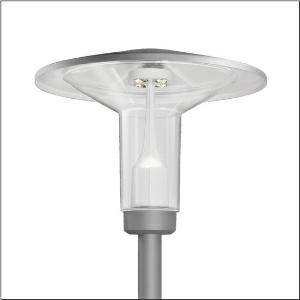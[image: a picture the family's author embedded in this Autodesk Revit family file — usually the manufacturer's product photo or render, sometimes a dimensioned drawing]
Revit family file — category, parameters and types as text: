
# Revit family: laterne_iq___st1_2a_5xa5255af14h_83bc
name_source: partatom
category: Lighting Fixtures
units: mm (PartAtom-declared; Revit-internal decimal feet)

## family parameters
Cut with Voids When Loaded = No
Host = Face
Light Source = No
Part Type = Normal
Room Calculation Point = No
Round Connector Dimension = Use Diameter
Shared = No

## types (1)
- --- (1 x LED, 1540 lm, 12.9 W, 2200K)
    Apparent Load = 13 VA
    CIE Flux Codes = 25 63 94 98 100
    Color Rendering = 70
    Color Temperature = 2200K
    Default Elevation = 1800 mm
    Description = Lantern iQ, mast luminaire, Module 540 iQ-SR, primary light control with 3 zone facetted reflector, of plastic, silver coated, highly specular, structured, primary optical cover: cover, of PMMA, transparent, light distribution: ST1.2a, light emission: direct distribution, primary light characteristic: asymmetric, installation type: post-top, LED, High Power LED, rated luminous flux: 1.540lm, luminous efficacy: 119lm/W, light colour: 722, colour temperature: 2200K, control gear: ECG iQ, control: presetting dimming logarithmic, Street-Remote, Auto-Match, Temp-Guard, Lumen-Switch, Night-Set, Smart-Wire, Light-Fading, Desk-Remote (wireless, voltage-free reading and setting of iQ features in the workshop via application-optimized NFC function/RFID function), optimised constant luminous flux control (CLO 2.0), with terminal, 6-pole, max. 2.5mm², mains connection: 230..240V, AC, 50/60Hz, start of lifetime: 13W, end of service life: 13W, reduction: 6W, luminaire housing, upper part, of glass-fibre reinforced polyester, coated, Siteco® metallic grey (DB 702S), diameter: 750mm, height: 583mm, spigot size: d x l = 76 x 70mm (post-top) | with reducer (optional accessory) 60 x 70mm, post-top mast mounting element, of diecast aluminium, coated, Siteco® metallic grey (DB 702S), Module 540 iQ-SR, traffic white (RAL 9016), equipment: standard, protection rating (complete): IP65, insulation class (complete): insulation class II (safety insulation), certification: CE, ENEC, VDE, packaging unit: 1 piece

Light Distribution: ST1.2a
    Height = 583 mm
    Lamp = 1 x LED
    Lamp Light Flux = 1540 lm
    Lamp Power = 12.9 W
    Lamp count = 1
    Length = 750 mm
    Luminous efficacy = 119 lm/W
    Manufacturer = Siteco
    ModVariant = No
    Model = 5XA5255AF14H
    Number of Poles = 1
    OnlyDefault = Yes
    Power Factor = 1
    Product Name = Laterne iQ | ST1.2a
    Product group = mast luminaire | pylon top
    ProductGroupID = 6100
    Protection Class = Protection class II
    Protection Degree = IP 65
    RLX_Detail_Level = 1
    RLX_Emergency_Light_Flux = 0 lm
    RLX_Emergency_Type = 0
    RLX_Emergency_Type_DB = No
    RlxData = <blob elided: 103969 chars, md5=67688b35>
    Socket = socket
    Standby Power = 0 W
    System Light Flux = 1540 lm
    System Power = 13 W
    Type Comments = factory setting: luminous flux: 100 % | dim-lin: 254 | 516 mA
    Type Image = l_1006050.jpg
    URL = http://relux.com
    VarID = @adj_092991
    Voltage = 0 V
    Weight = 0.00 kg
    Width = 0 mm  [stored 0 ft]

note: [stored X ft] marks values corroborated as IEEE doubles in the binary element streams (Revit-internal decimal feet)

## geometry (parser evidence)
native form markers: Blend x4, Sweep x11
no freeform markers — native parametric forms only
